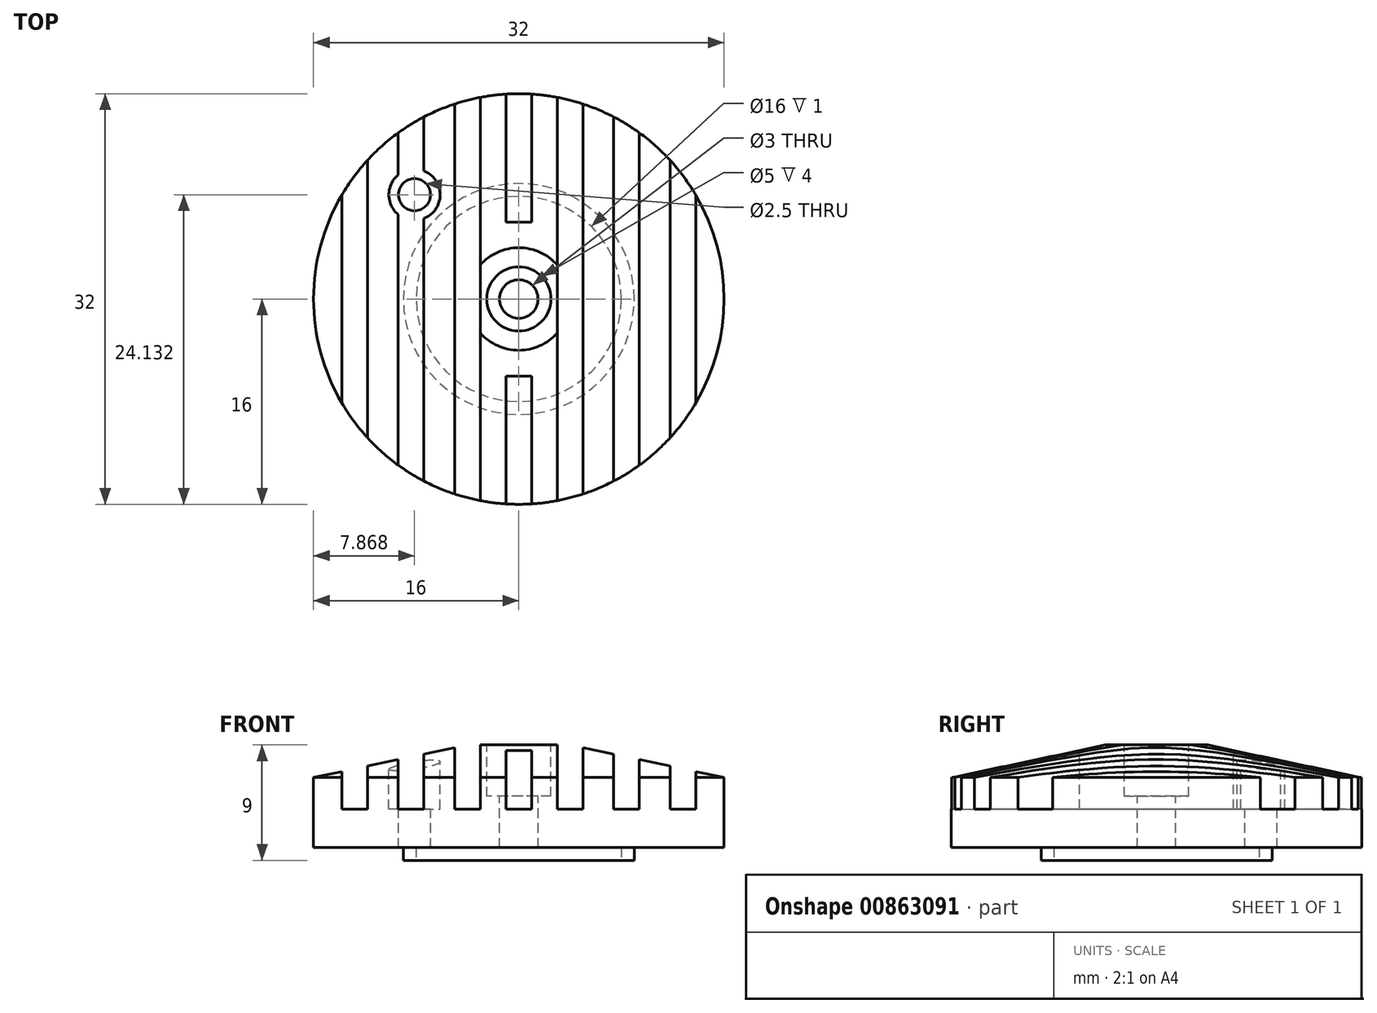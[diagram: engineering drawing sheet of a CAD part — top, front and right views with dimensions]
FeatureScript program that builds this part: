
annotation { "Feature Type Name" : "Feature", "Feature Type Description" : "" }
export const myFeature = defineFeature(function(context is Context, id is Id, definition is map)
    precondition{}
    {
        {
            var Q0;
            Q0=qCreatedBy(makeId("Front.planeOp"),FACE);
            var sketch = newSketch(context, id + "F0", { "sketchPlane" : qUnion([Q0])});
            skLineSegment(sketch, "E0", {"start": v(0, 0) * mm, "end": v(0, 8) * mm});
            skLineSegment(sketch, "E1", {"start": v(0, 8) * mm, "end": v(4, 8) * mm});
            skLineSegment(sketch, "E2", {"start": v(4, 8) * mm, "end": v(16, 5.45) * mm});
            skLineSegment(sketch, "E3", {"start": v(16, 5.45) * mm, "end": v(16, 0) * mm});
            skLineSegment(sketch, "E4", {"start": v(16, 0) * mm, "end": v(9, 0) * mm});
            skLineSegment(sketch, "E5", {"start": v(8, 0) * mm, "end": v(8, -1) * mm});
            skLineSegment(sketch, "E6", {"start": v(8, -1) * mm, "end": v(9, -1) * mm});
            skLineSegment(sketch, "E7", {"start": v(9, -1) * mm, "end": v(9, 0) * mm});
            skLineSegment(sketch, "E8.trimOffspring", {"start": v(8, 0) * mm, "end": v(0, 0) * mm});
            skSolve(sketch);
        }
        {
            var Q0;
            Q0=makeQuery(id+"F0.imprint","IMPRINT",FACE,{"disambiguationData":[TD([[makeQuery(id+"F0.imprint","IMPRINT",EDGE,{"derivedFrom":sQuery(id+"F0.wireOp",EDGE,"E0")}),-1.0]])]});
            var Q1;
            Q1=sQuery(id+"F0.wireOp",EDGE,"E0");
            revolve(context, id + "F1", {"surfaceOperationType" : NewSurfaceOperationType.NEW, "entities" : qUnion([Q0]), "axis" : qUnion([Q1]), "revolveType" : RevolveType.FULL});
        }
        {
            var Q0;
            Q0=makeQuery(id+"F1.opRevolve","SWEPT_FACE",FACE,{"disambiguationData":[OSD([sQuery(id+"F0.wireOp",EDGE,"E1")])]});
            var sketch = newSketch(context, id + "F2", { "sketchPlane" : qUnion([Q0])});
            skPoint(sketch, "E9", {"position": v(0, 0) * mm});
            skLineSegment(sketch, "E10", {"start": v(0, 0) * mm, "end": v(-8.13, 8.13) * mm, "construction": true});
            skSolve(sketch);
        }
        {
            var Q0;
            Q0=sQuery(id+"F2.wireOp",VERTEX,"E9");
            var Q1;
            Q1=makeQuery(id+"F1.opRevolve","SWEPT_BODY",BODY,{"disambiguationData":[OSD([sQuery(id+"F0.wireOp",EDGE,"E0"),sQuery(id+"F0.wireOp",EDGE,"E1"),sQuery(id+"F0.wireOp",EDGE,"E2"),sQuery(id+"F0.wireOp",EDGE,"E3"),sQuery(id+"F0.wireOp",EDGE,"E4")])]});
            hole(context, id + "F3", {"style" : HoleStyle.C_BORE, "endStyle" : HoleEndStyle.THROUGH, "holeDiameter" : 3 * mm, "cBoreDiameter" : 5 * mm, "cBoreDepth" : 4 * mm, "majorDiameter" : 5 * mm, "isTappedThrough" : true, "tappedDepth" : 6.5 * mm, "tapClearance" : 3, "startFromSketch" : true, "locations" : qUnion([Q0]), "scope" : qUnion([Q1])});
        }
        {
            var Q0;
            Q0=sQuery(id+"F2.wireOp",VERTEX,"E10.end");
            var Q1;
            Q1=makeQuery(id+"F1.opRevolve","SWEPT_BODY",BODY,{"disambiguationData":[OSD([sQuery(id+"F0.wireOp",EDGE,"E0"),sQuery(id+"F0.wireOp",EDGE,"E1"),sQuery(id+"F0.wireOp",EDGE,"E2"),sQuery(id+"F0.wireOp",EDGE,"E3"),sQuery(id+"F0.wireOp",EDGE,"E4")])]});
            hole(context, id + "F4", {"style" : HoleStyle.C_BORE, "endStyle" : HoleEndStyle.THROUGH, "holeDiameter" : 2.5 * mm, "cBoreDiameter" : 4 * mm, "cBoreDepth" : 5 * mm, "majorDiameter" : 5 * mm, "isTappedThrough" : true, "tappedDepth" : 6.5 * mm, "tapClearance" : 3, "startFromSketch" : true, "locations" : qUnion([Q0]), "scope" : qUnion([Q1])});
        }
        {
            var Q0;
            Q0=makeQuery(id+"F1.opRevolve","SWEPT_FACE",FACE,{"disambiguationData":[OSD([sQuery(id+"F0.wireOp",EDGE,"E1")])]});
            var sketch = newSketch(context, id + "F5", { "sketchPlane" : qUnion([Q0])});
            skLineSegment(sketch, "E11.bottom", {"start": v(-3, -17.5) * mm, "end": v(-5, -17.5) * mm});
            skLineSegment(sketch, "E11.top", {"start": v(-3, 17.5) * mm, "end": v(-5, 17.5) * mm});
            skLineSegment(sketch, "E11.left", {"start": v(-3, -17.5) * mm, "end": v(-3, 17.5) * mm});
            skLineSegment(sketch, "E11.right", {"start": v(-5, -17.5) * mm, "end": v(-5, 17.5) * mm});
            skPoint(sketch, "E11.middle", {"position": v(-4, 0) * mm});
            skLineSegment(sketch, "E12.bottom", {"start": v(-7.4, 17.5) * mm, "end": v(-9.4, 17.5) * mm});
            skLineSegment(sketch, "E12.top", {"start": v(-7.4, -17.5) * mm, "end": v(-9.4, -17.5) * mm});
            skLineSegment(sketch, "E12.left", {"start": v(-7.4, 17.5) * mm, "end": v(-7.4, -17.5) * mm});
            skLineSegment(sketch, "E12.right", {"start": v(-9.4, 17.5) * mm, "end": v(-9.4, -17.5) * mm});
            skPoint(sketch, "E12.middle", {"position": v(-8.4, 0) * mm});
            skPoint(sketch, "E12.cornerSnap0", {"position": v(-4, 17.5) * mm});
            skLineSegment(sketch, "E13.bottom", {"start": v(-11.8, 17.5) * mm, "end": v(-13.8, 17.5) * mm});
            skLineSegment(sketch, "E13.top", {"start": v(-11.8, -17.5) * mm, "end": v(-13.8, -17.5) * mm});
            skLineSegment(sketch, "E13.left", {"start": v(-11.8, 17.5) * mm, "end": v(-11.8, -17.5) * mm});
            skLineSegment(sketch, "E13.right", {"start": v(-13.8, 17.5) * mm, "end": v(-13.8, -17.5) * mm});
            skPoint(sketch, "E13.middle", {"position": v(-12.8, 0) * mm});
            skLineSegment(sketch, "E14.MirrorCS", {"start": v(3, 17.5) * mm, "end": v(5, 17.5) * mm});
            skLineSegment(sketch, "E15.MirrorCS", {"start": v(3, -17.5) * mm, "end": v(3, 17.5) * mm});
            skLineSegment(sketch, "E16.MirrorCS", {"start": v(5, -17.5) * mm, "end": v(5, 17.5) * mm});
            skLineSegment(sketch, "E17.MirrorCS", {"start": v(7.4, 17.5) * mm, "end": v(9.4, 17.5) * mm});
            skLineSegment(sketch, "E18.MirrorCS", {"start": v(7.4, 17.5) * mm, "end": v(7.4, -17.5) * mm});
            skLineSegment(sketch, "E19.MirrorCS", {"start": v(9.4, 17.5) * mm, "end": v(9.4, -17.5) * mm});
            skLineSegment(sketch, "E20.MirrorCS", {"start": v(11.8, 17.5) * mm, "end": v(13.8, 17.5) * mm});
            skLineSegment(sketch, "E21.MirrorCS", {"start": v(13.8, 17.5) * mm, "end": v(13.8, -17.5) * mm});
            skLineSegment(sketch, "E22.MirrorCS", {"start": v(11.8, 17.5) * mm, "end": v(11.8, -17.5) * mm});
            skLineSegment(sketch, "E23.MirrorCS", {"start": v(3, -17.5) * mm, "end": v(5, -17.5) * mm});
            skLineSegment(sketch, "E24.MirrorCS", {"start": v(7.4, -17.5) * mm, "end": v(9.4, -17.5) * mm});
            skLineSegment(sketch, "E25.MirrorCS", {"start": v(11.8, -17.5) * mm, "end": v(13.8, -17.5) * mm});
            skLineSegment(sketch, "E26.bottom", {"start": v(1, 17.5) * mm, "end": v(-1, 17.5) * mm});
            skLineSegment(sketch, "E26.top", {"start": v(1, 6) * mm, "end": v(-1, 6) * mm});
            skLineSegment(sketch, "E26.left", {"start": v(1, 17.5) * mm, "end": v(1, 6) * mm});
            skLineSegment(sketch, "E26.right", {"start": v(-1, 17.5) * mm, "end": v(-1, 6) * mm});
            skPoint(sketch, "E26.middle", {"position": v(0, 11.75) * mm});
            skPoint(sketch, "E26.cornerSnap0", {"position": v(4, 17.5) * mm});
            skLineSegment(sketch, "E27.MirrorCS", {"start": v(1, -6) * mm, "end": v(-1, -6) * mm});
            skLineSegment(sketch, "E28.MirrorCS", {"start": v(1, -17.5) * mm, "end": v(1, -6) * mm});
            skLineSegment(sketch, "E29.MirrorCS", {"start": v(-1, -17.5) * mm, "end": v(-1, -6) * mm});
            skLineSegment(sketch, "E30.MirrorCS", {"start": v(1, -17.5) * mm, "end": v(-1, -17.5) * mm});
            skSolve(sketch);
        }
        {
            var Q0;
            Q0 = qSketchRegion(id + "F5", true);
            extrude(context, id + "F6", {"entities" : qUnion([Q0]), "operationType" : NewBodyOperationType.REMOVE, "oppositeDirection" : true, "depth" : 5 * mm, "offsetDistance" : 25 * mm});
        }
    });
